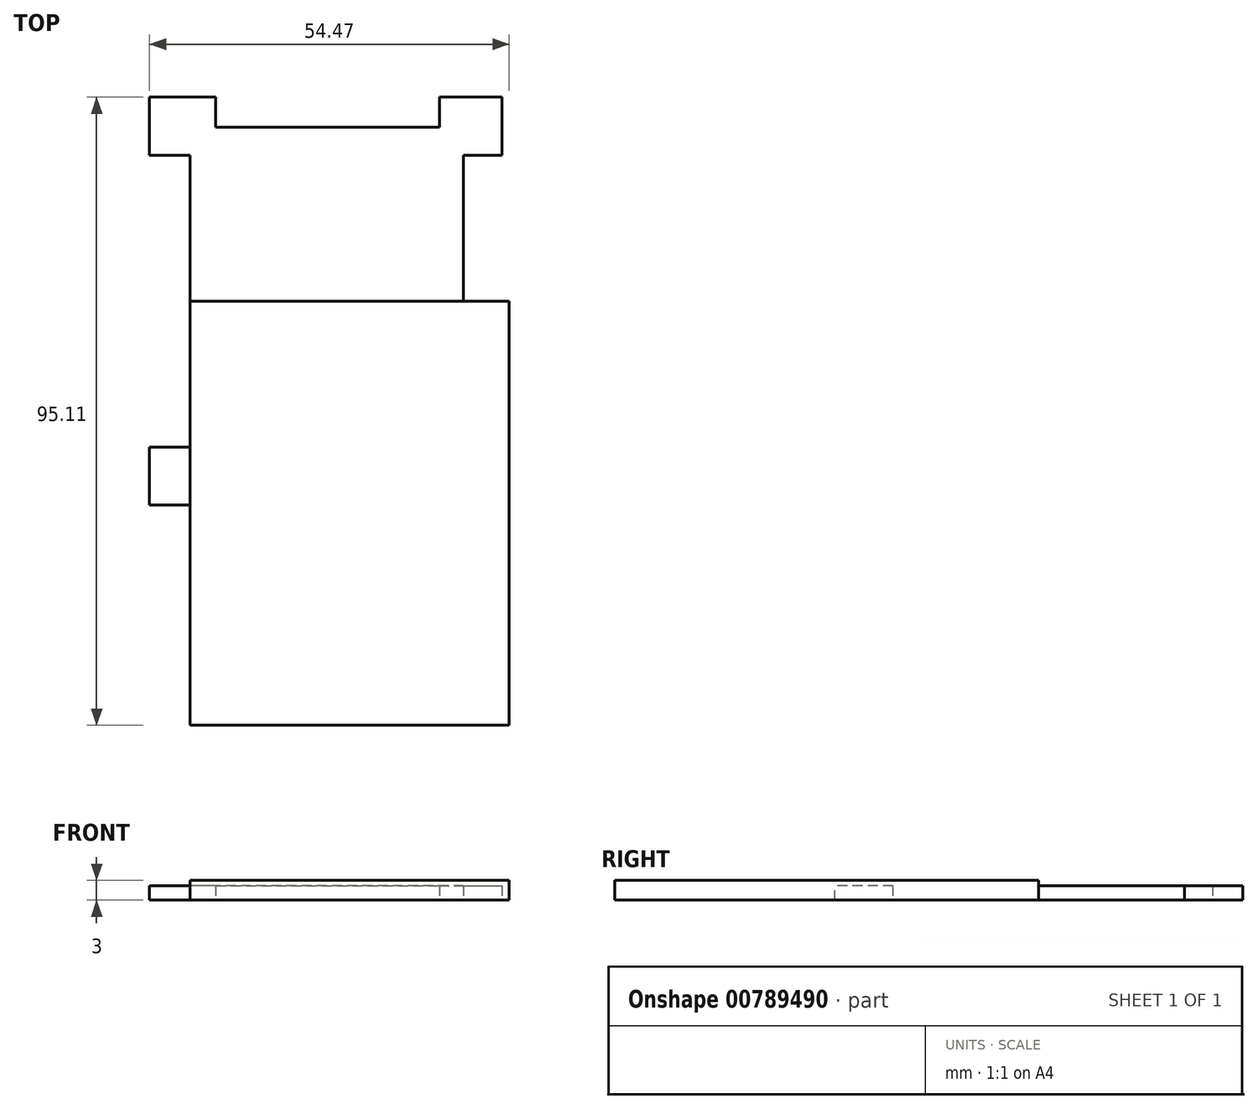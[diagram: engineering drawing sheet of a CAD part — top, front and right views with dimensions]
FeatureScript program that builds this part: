
annotation { "Feature Type Name" : "Feature", "Feature Type Description" : "" }
export const myFeature = defineFeature(function(context is Context, id is Id, definition is map)
    precondition{}
    {
        {
            var Q0;
            Q0=qCreatedBy(makeId("Top.planeOp"),FACE);
            var sketch = newSketch(context, id + "F0", { "sketchPlane" : qUnion([Q0])});
            skLineSegment(sketch, "E0", {"start": v(0, -64.2) * mm, "end": v(48.37, -64.2) * mm});
            skLineSegment(sketch, "E1", {"start": v(48.37, -64.2) * mm, "end": v(48.37, 0) * mm});
            skLineSegment(sketch, "E2", {"start": v(48.37, 0) * mm, "end": v(0, 0) * mm});
            skLineSegment(sketch, "E3", {"start": v(0, 0) * mm, "end": v(0, -64.2) * mm});
            skLineSegment(sketch, "E4", {"start": v(48.37, 12.73) * mm, "end": v(61.06, 12.73) * mm});
            skLineSegment(sketch, "E5", {"start": v(61.06, 12.73) * mm, "end": v(61.06, 0) * mm});
            skLineSegment(sketch, "E6", {"start": v(61.06, 0) * mm, "end": v(48.37, 0) * mm});
            skLineSegment(sketch, "E7", {"start": v(48.37, 12.73) * mm, "end": v(48.37, 0) * mm});
            skLineSegment(sketch, "E8", {"start": v(60.95, -64.2) * mm, "end": v(60.95, -77.19) * mm});
            skLineSegment(sketch, "E9", {"start": v(60.95, -77.19) * mm, "end": v(48.89, -77.19) * mm});
            skLineSegment(sketch, "E10", {"start": v(48.89, -77.19) * mm, "end": v(48.37, -64.2) * mm});
            skLineSegment(sketch, "E11", {"start": v(48.37, -64.2) * mm, "end": v(60.95, -64.2) * mm});
            skSolve(sketch);
        }
        {
            var Q0;
            Q0=makeQuery(id+"F0.imprint","IMPRINT",FACE,{"disambiguationData":[TD([[makeQuery(id+"F0.imprint","IMPRINT",EDGE,{"derivedFrom":sQuery(id+"F0.wireOp",EDGE,"E0")}),1.0]])]});
            var Q1;
            Q1=makeQuery(id+"F0.imprint","IMPRINT",FACE,{"disambiguationData":[TD([[makeQuery(id+"F0.imprint","IMPRINT",EDGE,{"derivedFrom":sQuery(id+"F0.wireOp",EDGE,"E8")}),-1.0]])]});
            var Q2;
            Q2=makeQuery(id+"F0.imprint","IMPRINT",FACE,{"disambiguationData":[TD([[makeQuery(id+"F0.imprint","IMPRINT",EDGE,{"derivedFrom":sQuery(id+"F0.wireOp",EDGE,"E4")}),-1.0]])]});
            extrude(context, id + "F1", {"entities" : qUnion([Q0, Q1, Q2]), "depth" : 3 * mm, "offsetDistance" : 25 * mm});
        }
        {
            var Q0;
            Q0=makeQuery(id+"F1.opExtrude","SWEPT_BODY",BODY,{"disambiguationData":[OSD([sQuery(id+"F0.wireOp",EDGE,"E4"),sQuery(id+"F0.wireOp",EDGE,"E5"),sQuery(id+"F0.wireOp",EDGE,"E6"),sQuery(id+"F0.wireOp",EDGE,"E7")])]});
            deleteBodies(context, id + "F2", {"entities" : qUnion([Q0])});
        }
        {
            var Q0;
            Q0=makeQuery(id+"F1.opExtrude","SWEPT_BODY",BODY,{"disambiguationData":[OSD([sQuery(id+"F0.wireOp",EDGE,"E8"),sQuery(id+"F0.wireOp",EDGE,"E9"),sQuery(id+"F0.wireOp",EDGE,"E10"),sQuery(id+"F0.wireOp",EDGE,"E11")])]});
            deleteBodies(context, id + "F3", {"entities" : qUnion([Q0])});
        }
        {
            var Q0;
            Q0=qCreatedBy(makeId("Top.planeOp"),FACE);
            var sketch = newSketch(context, id + "F4", { "sketchPlane" : qUnion([Q0])});
            skLineSegment(sketch, "E12.bottom", {"start": v(0, 0) * mm, "end": v(41.45, 0) * mm});
            skLineSegment(sketch, "E12.top", {"start": v(0, 26.34) * mm, "end": v(41.45, 26.34) * mm});
            skLineSegment(sketch, "E12.left", {"start": v(0, 0) * mm, "end": v(0, 26.34) * mm});
            skLineSegment(sketch, "E12.right", {"start": v(41.45, 0) * mm, "end": v(41.45, 26.34) * mm});
            skLineSegment(sketch, "E13.bottom", {"start": v(37.8, 22.1) * mm, "end": v(47.26, 22.1) * mm});
            skLineSegment(sketch, "E13.top", {"start": v(37.8, 30.9) * mm, "end": v(47.26, 30.9) * mm});
            skLineSegment(sketch, "E13.left", {"start": v(37.8, 22.1) * mm, "end": v(37.8, 30.9) * mm});
            skLineSegment(sketch, "E13.right", {"start": v(47.26, 22.1) * mm, "end": v(47.26, 30.9) * mm});
            skLineSegment(sketch, "E14.bottom", {"start": v(3.92, 22.1) * mm, "end": v(-6.1, 22.1) * mm});
            skLineSegment(sketch, "E14.top", {"start": v(3.92, 30.9) * mm, "end": v(-6.1, 30.9) * mm});
            skLineSegment(sketch, "E14.left", {"start": v(3.92, 22.1) * mm, "end": v(3.92, 30.9) * mm});
            skLineSegment(sketch, "E14.right", {"start": v(-6.1, 22.1) * mm, "end": v(-6.1, 30.9) * mm});
            skSolve(sketch);
        }
        {
            var Q0;
            {var subQ1=sQuery(id+"F4.wireOp",EDGE,"E12.bottom");Q0=makeQuery(id+"F4.imprint","IMPRINT",FACE,{"disambiguationData":[TD([[makeQuery(id+"F4.imprint","IMPRINT",EDGE,{"derivedFrom":subQ1}),1.0]])]});}
            var Q1;
            {var subQ6=sQuery(id+"F4.wireOp",EDGE,"E14.top");Q1=makeQuery(id+"F4.imprint","IMPRINT",FACE,{"disambiguationData":[TD([[makeQuery(id+"F4.imprint","IMPRINT",EDGE,{"derivedFrom":subQ6}),1.0]])]});}
            var Q2;
            {var subQ0=sQuery(id+"F4.wireOp",EDGE,"E12.left");var subQ1=sQuery(id+"F4.wireOp",EDGE,"E12.top");var subQ2=makeQuery(id+"F4.imprint","INTERSECT",VERTEX,{"derivedFrom":[subQ1,subQ0]});Q2=makeQuery(id+"F4.imprint","IMPRINT",FACE,{"disambiguationData":[TD([[makeQuery(id+"F4.imprint","IMPRINT",EDGE,{"disambiguationData":[TD([[subQ2,-1.0]])],"derivedFrom":subQ1}),-1.0]])]});}
            var Q3;
            {var subQ0=sQuery(id+"F4.wireOp",EDGE,"E12.right");var subQ1=sQuery(id+"F4.wireOp",EDGE,"E12.top");var subQ2=makeQuery(id+"F4.imprint","INTERSECT",VERTEX,{"derivedFrom":[subQ1,subQ0]});Q3=makeQuery(id+"F4.imprint","IMPRINT",FACE,{"disambiguationData":[TD([[makeQuery(id+"F4.imprint","IMPRINT",EDGE,{"disambiguationData":[TD([[subQ2,1.0]])],"derivedFrom":subQ1}),-1.0]])]});}
            var Q4;
            {var subQ0=sQuery(id+"F4.wireOp",EDGE,"E13.top");Q4=makeQuery(id+"F4.imprint","IMPRINT",FACE,{"disambiguationData":[TD([[makeQuery(id+"F4.imprint","IMPRINT",EDGE,{"derivedFrom":subQ0}),-1.0]])]});}
            extrude(context, id + "F5", {"entities" : qUnion([Q0, Q1, Q2, Q3, Q4]), "depth" : 2.18 * mm, "offsetDistance" : 25 * mm});
        }
        {
            var Q0;
            Q0=makeQuery(id+"F5.opExtrude","CAP_FACE",FACE,{"disambiguationData":[OSD([sQuery(id+"F4.wireOp",EDGE,"E12.bottom"),sQuery(id+"F4.wireOp",EDGE,"E12.top"),sQuery(id+"F4.wireOp",EDGE,"E12.left"),sQuery(id+"F4.wireOp",EDGE,"E12.right"),sQuery(id+"F4.wireOp",EDGE,"E13.bottom"),sQuery(id+"F4.wireOp",EDGE,"E13.top"),sQuery(id+"F4.wireOp",EDGE,"E13.left"),sQuery(id+"F4.wireOp",EDGE,"E13.right"),sQuery(id+"F4.wireOp",EDGE,"E14.bottom"),sQuery(id+"F4.wireOp",EDGE,"E14.top"),sQuery(id+"F4.wireOp",EDGE,"E14.left"),sQuery(id+"F4.wireOp",EDGE,"E14.right")])],"isStart":false});
            var sketch = newSketch(context, id + "F6", { "sketchPlane" : qUnion([Q0])});
            skSolve(sketch);
        }
        {
            var Q0;
            Q0=makeQuery(id+"F6.imprint","IMPRINT",FACE,{"disambiguationData":[TD([[makeQuery(id+"F6.imprint","IMPRINT",EDGE,{"derivedFrom":makeQuery(id+"F5.opExtrude","CAP_EDGE",EDGE,{"disambiguationData":[OSD([sQuery(id+"F4.wireOp",EDGE,"E12.bottom")])],"isStart":false})}),1.0]])]});
            var sketch = newSketch(context, id + "F7", { "sketchPlane" : qUnion([Q0])});
            skSolve(sketch);
        }
        {
            var Q0;
            Q0=makeQuery(id+"F5.opExtrude","SWEPT_BODY",BODY,{"disambiguationData":[OSD([sQuery(id+"F4.wireOp",EDGE,"E12.bottom"),sQuery(id+"F4.wireOp",EDGE,"E12.top"),sQuery(id+"F4.wireOp",EDGE,"E12.left"),sQuery(id+"F4.wireOp",EDGE,"E12.right"),sQuery(id+"F4.wireOp",EDGE,"E13.bottom"),sQuery(id+"F4.wireOp",EDGE,"E13.top"),sQuery(id+"F4.wireOp",EDGE,"E13.left"),sQuery(id+"F4.wireOp",EDGE,"E13.right"),sQuery(id+"F4.wireOp",EDGE,"E14.bottom"),sQuery(id+"F4.wireOp",EDGE,"E14.top"),sQuery(id+"F4.wireOp",EDGE,"E14.left"),sQuery(id+"F4.wireOp",EDGE,"E14.right")])]});
            var Q1;
            Q1=qCreatedBy(makeId("Front.planeOp"),FACE);
            mirror(context, id + "F8", {"operationType" : NewBodyOperationType.ADD, "entities" : qUnion([Q0]), "mirrorPlane" : qUnion([Q1])});
        }
    });
